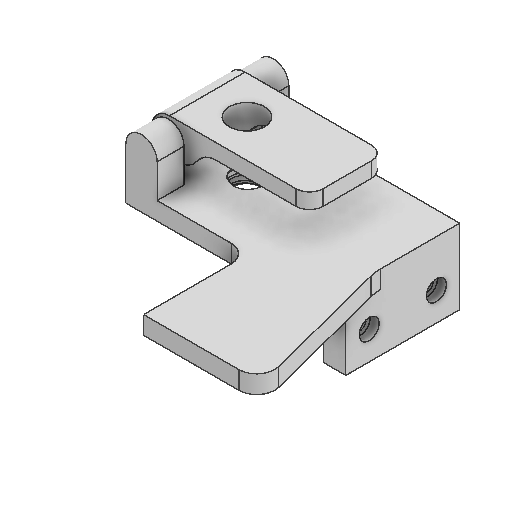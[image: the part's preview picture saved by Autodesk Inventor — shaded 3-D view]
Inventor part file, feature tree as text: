
AUTODESK INVENTOR PART (.ipt)
format: ipt  version: 2025 (Build 290162000, 162)  size: 616,448 bytes
history: native  units: mm
features: projected_geometry x27, sketch x26, extrude x24, fillet x9, plane x7, mirror x2, helix x1
ambient origin geometry x8: Origin, YZ Plane, XZ Plane, XY Plane, X Axis, Y Axis, Z Axis, Center Point
bodies: Solid1 (feature_tree)
feature tree (96):
  extrude  "Extrusion1"  Depth=152.4mm
  plane  "Work Plane1"
  extrude  "Extrusion2"  [1 undecoded]
  extrude  "Extrusion3"  Depth=0.25mm
  extrude  "Extrusion4"  Depth=25.4mm
  fillet  "Fillet1"  Radius=2.75mm
  extrude  "Extrusion5"  Depth=10.0mm TaperAngle=0.0deg
  extrude  "Extrusion6"  Depth=10.0mm
  extrude  "Extrusion7"  Depth=8.0mm TaperAngle=0.0deg
  extrude  "Extrusion8"  Depth=10.0mm TaperAngle=0.0deg
  extrude  "Extrusion9"  Depth=25.4mm TaperAngle=0.0deg
  extrude  "Extrusion10"  Depth=14.0mm
  extrude  "Extrusion11"  Depth=8.0mm
  plane  "Work Plane2"
  extrude  "Extrusion12"  Depth=15.0mm
  mirror  "Mirror1"
  plane  "Work Plane3"
  sketch  "Sketch13"  dims[d37=0.5mm d38=0.5mm]
  plane  "Work Plane4"
  extrude  "Extrusion13"  Depth=0.5mm
  extrude  "Extrusion14"  Depth=0.5mm
  fillet  "Fillet2"  Radius=55.0mm
  fillet  "Fillet3"  [1 undecoded]
  extrude  "Extrusion15"  Depth=10.0mm
  extrude  "Extrusion16"  TaperAngle=0.0deg  [1 undecoded]
  fillet  "Fillet5"  Radius=1.5mm
  extrude  "Extrusion17"  Depth=6.0mm
  extrude  "Extrusion18"  Depth=20.0mm TaperAngle=0.0deg
  fillet  "Fillet6"  Radius=6.0mm
  fillet  "Fillet7"  Radius=6.0mm
  plane  "Work Plane5"
  helix  "Coil2"  [1 undecoded]
  plane  "Work Plane6"
  extrude  "Extrusion19"  Depth=10.0mm
  fillet  "Fillet8"  Radius=61.0mm
  sketch  "Sketch21"  dims[d84=0.0mm d85=0.0mm d86=2.0mm]
  sketch  "Sketch22"  dims[d87=0.0mm d88=0.0mm d89=8.0mm d90=0.0mm]
  extrude  "Extrusion20"  Depth=2.5mm
  extrude  "Extrusion21"  Depth=2.0mm
  extrude  "Extrusion22"  Depth=8.0mm TaperAngle=0.0deg
  extrude  "Extrusion23"  Depth=10.0mm
  extrude  "Extrusion24"  Depth=10.0mm TaperAngle=0.0deg
  plane  "Work Plane7"
  mirror  "Mirror2"
  fillet  "Fillet9"  Radius=50.8mm
  fillet  "Fillet10"  Radius=30.0mm
  sketch  "Sketch1"  dims[d0=25.4mm d1=152.4mm]
  sketch  "Sketch2"  dims[d2=10.0mm d3=0.0mm d4=-50.8mm]
  projected_geometry  "Projected Loop1"
  sketch  "Sketch3"  dims[d5=25.4mm d6=0.25mm]
  projected_geometry  "Projected Loop2"
  sketch  "Sketch4"  dims[d7=50.8mm d8=0.0mm d9=25.4mm d10=2.75mm]
  sketch  "Sketch5"  dims[d11=35.45mm d12=0.0mm d13=10.0mm d14=0.0mm]
  projected_geometry  "Projected Loop3"
  sketch  "Sketch6"  dims[d15=10.0mm d16=55.0mm]
  projected_geometry  "Projected Loop4"
  sketch  "Sketch7"  dims[d17=55.0mm d18=8.0mm d19=0.0mm]
  projected_geometry  "Projected Loop5"
  sketch  "Sketch8"  dims[d20=0.0mm d21=0.0mm d22=10.0mm d23=0.0mm]
  projected_geometry  "Projected Loop6"
  sketch  "Sketch9"  dims[d24=25.4mm d25=0.0mm d26=25.4mm d27=0.0mm]
  projected_geometry  "Projected Loop7"
  sketch  "Sketch10"  dims[d28=55.0mm d29=0.0mm d30=14.0mm]
  projected_geometry  "Projected Loop8"
  sketch  "Sketch11"  dims[d31=12.0mm d32=0.0mm d33=8.0mm]
  projected_geometry  "Projected Loop9"
  sketch  "Sketch12"  dims[d34=12.0mm d35=0.0mm d36=15.0mm]
  projected_geometry  "Projected Loop10"
  projected_geometry  "Projected Loop11"
  sketch  "Sketch14"  dims[d39=16.0mm d40=0.5mm d41=55.0mm d42=0.0mm d43=0.0mm d44=0.0mm]
  projected_geometry  "Projected Loop12"
  sketch  "Sketch15"  dims[d45=10.0mm d46=8.0mm]
  projected_geometry  "Projected Loop13"
  sketch  "Sketch16"  dims[d48=12.7mm d49=0.0mm d50=0.0mm d53=1.5mm]
  sketch  "Sketch17"  dims[d54=15.0mm d55=0.0mm d56=6.0mm]
  projected_geometry  "Projected Loop14"
  sketch  "Sketch18"  dims[d57=20.0mm d58=0.0mm d59=20.0mm d60=0.0mm d61=6.0mm d62=6.0mm d71=2.0mm]
  projected_geometry  "Projected Loop15"
  sketch  "Sketch19"  dims[d72=3.0mm d73=10.0mm d74=50.0mm d75=0.0mm d76=90.0deg d77=90.0deg d78=0.0mm d79=0.0mm d80=6.35mm d81=61.0mm]
  projected_geometry  "Projected Loop16"
  sketch  "Sketch20"  dims[d82=2.5mm d83=2.5mm]
  projected_geometry  "Projected Loop17"
  projected_geometry  "Projected Loop19"
  projected_geometry  "Projected Loop20"
  projected_geometry  "Projected Loop21"
  projected_geometry  "Projected Loop22"
  projected_geometry  "Projected Loop23"
  projected_geometry  "Projected Loop24"
  sketch  "Sketch23"  dims[d91=45.4mm d92=10.0mm]
  projected_geometry  "Projected Loop25"
  sketch  "Sketch24"  dims[d93=10.0mm d95=25.4mm d96=0.0mm d97=50.8mm d98=30.0mm]
  projected_geometry  "Projected Loop26"
  sketch  "Sketch25"  dims[d99=2.6mm]
  projected_geometry  "Projected Loop27"
  sketch  "Sketch26"  dims[d100=0.0mm d101=0.0mm d102=9.0mm d103=4.0mm d104=0.0mm d105=20.0mm d106=10.0mm]
  projected_geometry  "Projected Loop28"
note: 4 required parameter values undecoded (feature->parameter linkage not recoverable at this tier; creation-order binding heuristic only, values carry confidence <= 0.55)
